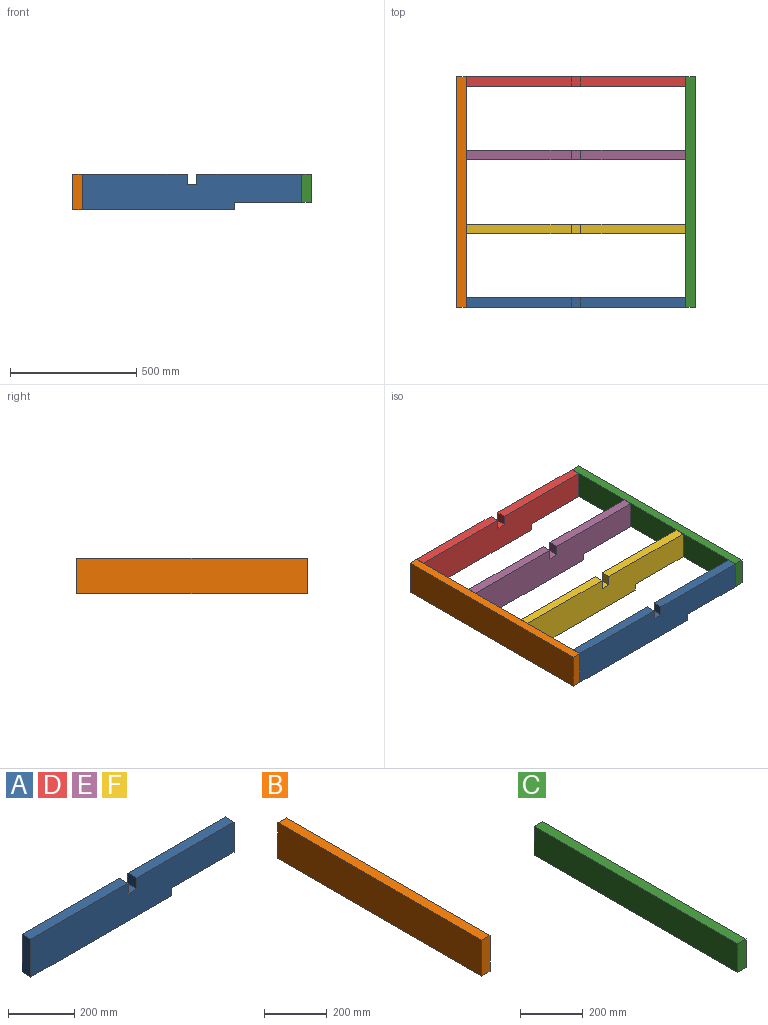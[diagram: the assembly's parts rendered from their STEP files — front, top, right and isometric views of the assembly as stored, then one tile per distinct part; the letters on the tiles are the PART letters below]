
ASSEMBLY  parts=6 mates=6
PART A: 12 faces, bbox 870x38.1x139.7 mm
  f0: plane 415.93x38.1mm, normal (0,0,1), area 15846.7mm2, adj f5,f7,f8,f11
  f1: plane 139.7x38.1mm, normal (-1,0,0), area 5322.6mm2, adj f2,f6,f7,f8
  f2: plane 603.24x38.1mm, normal (0,0,-1), area 22983.6mm2, adj f1,f3,f7,f8
  f3: plane 38.1x28.29mm, normal (1,0,0), area 1077.9mm2, adj f2,f4,f7,f8
  f4: plane 266.71x38.1mm, normal (0,0,-1), area 10161.5mm2, adj f3,f5,f7,f8
  f5: plane 111.41x38.1mm, normal (1,0,0), area 4244.6mm2, adj f0,f4,f7,f8
  f6: plane 415.93x38.1mm, normal (0,0,1), area 15846.7mm2, adj f1,f7,f8,f10
  f7: plane 869.95x139.7mm, normal (0,1,0), area 112472.9mm2, adj f0,f1,f2,f3,f4,f5,f6,f9
  f8: plane 869.95x139.7mm, normal (0,-1,0), area 112472.9mm2, adj f0,f1,f2,f3,f4,f5,f6,f9
  f9: plane 38.1x38.1mm, normal (0,0,1), area 1451.6mm2, adj f7,f8,f10,f11
  f10: plane 39.72x38.1mm, normal (1,0,0), area 1513.4mm2, adj f6,f7,f8,f9
  f11: plane 39.72x38.1mm, normal (-1,0,0), area 1513.4mm2, adj f0,f7,f8,f9
PART B: 6 faces, bbox 38.1x914.4x139.7 mm
  f0: plane 914.4x139.7mm, normal (1,0,0), area 127741.7mm2, adj f1,f3,f4,f5
  f1: plane 914.4x38.1mm, normal (0,0,1), area 34838.6mm2, adj f0,f2,f4,f5
  f2: plane 914.4x139.7mm, normal (-1,0,0), area 127741.7mm2, adj f1,f3,f4,f5
  f3: plane 914.4x38.1mm, normal (0,0,-1), area 34838.6mm2, adj f0,f2,f4,f5
  f4: plane 139.7x38.1mm, normal (0,1,0), area 5322.6mm2, adj f0,f1,f2,f3
  f5: plane 139.7x38.1mm, normal (0,-1,0), area 5322.6mm2, adj f0,f1,f2,f3
PART C: 6 faces, bbox 38.1x914.4x111.4 mm
  f0: plane 914.4x111.41mm, normal (-1,0,0), area 101871.3mm2, adj f1,f3,f4,f5
  f1: plane 914.4x38.1mm, normal (0,0,-1), area 34838.6mm2, adj f0,f2,f4,f5
  f2: plane 914.4x111.41mm, normal (1,0,0), area 101871.3mm2, adj f1,f3,f4,f5
  f3: plane 914.4x38.1mm, normal (0,0,1), area 34838.6mm2, adj f0,f2,f4,f5
  f4: plane 111.41x38.1mm, normal (0,1,0), area 4244.6mm2, adj f0,f1,f2,f3
  f5: plane 111.41x38.1mm, normal (0,-1,0), area 4244.6mm2, adj f0,f1,f2,f3
PART D: same geometry as A
PART E: same geometry as A
PART F: same geometry as A
PLACE A t=(553.24,207.53,-109.75)mm
PLACE B t=(553.24,207.53,-109.75)mm
PLACE C t=(553.24,207.53,-109.75)mm fixed
PLACE D t=(553.24,1083.83,-109.75)mm
PLACE E t=(553.24,791.73,-109.75)mm
PLACE F t=(553.24,499.63,-109.75)mm
MATE planar C.f3 <-> A.f6  axis (0,0,1) through (-690.99,-275.07,255.66)mm
MATE planar B.f5 <-> A.f8  axis (0,-1,0) through (-1599.04,-732.27,185.81)mm
MATE planar B.f0 <-> A.f1  axis (1,0,0) through (-1579.99,-275.07,185.81)mm
MATE planar C.f0 <-> F.f5  axis (-1,0,0) through (-710.04,-275.07,199.95)mm
MATE planar C.f5 <-> A.f8  axis (0,-1,0) through (-690.99,-732.27,199.95)mm
MATE planar B.f1 <-> A.f6  axis (0,0,1) through (-1599.04,-275.07,255.66)mm
